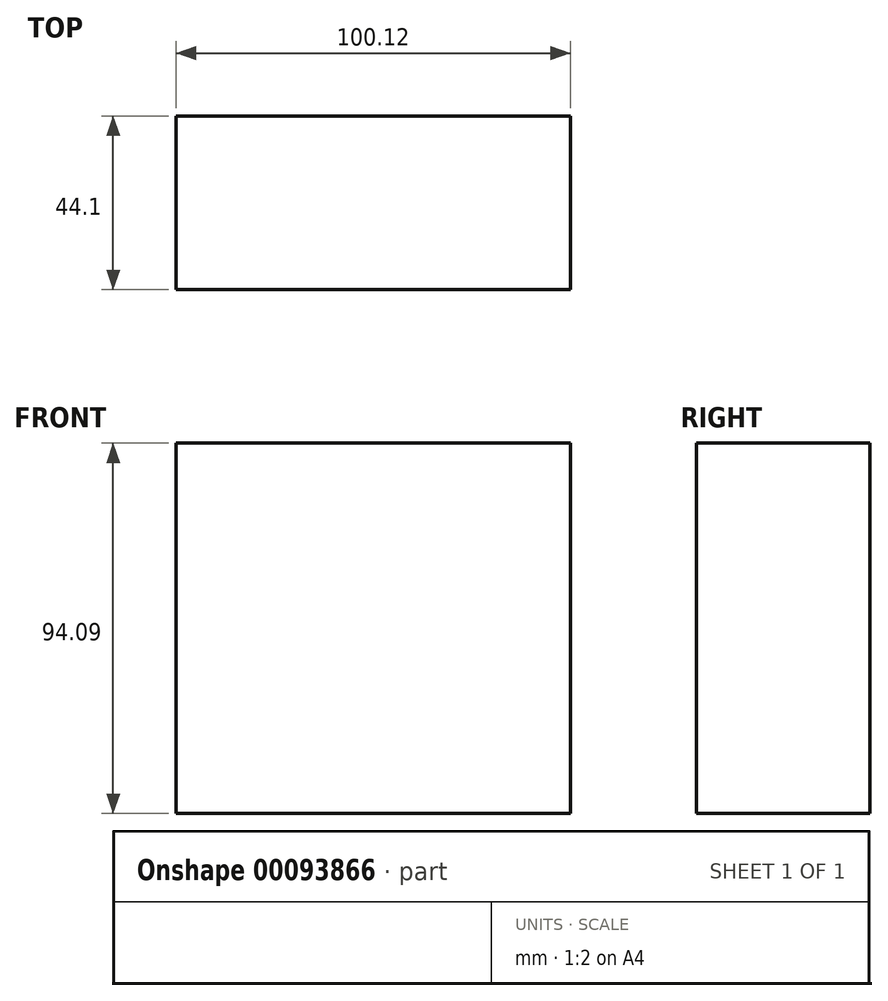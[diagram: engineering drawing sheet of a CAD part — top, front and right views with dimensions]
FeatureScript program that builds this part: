
annotation { "Feature Type Name" : "Feature", "Feature Type Description" : "" }
export const myFeature = defineFeature(function(context is Context, id is Id, definition is map)
    precondition{}
    {
        {
            var Q0;
            Q0=qCreatedBy(makeId("Top.planeOp"),FACE);
            var sketch = newSketch(context, id + "F0", { "sketchPlane" : qUnion([Q0])});
            skLineSegment(sketch, "E0.bottom", {"start": v(-26.52, 23.99) * mm, "end": v(73.6, 23.99) * mm});
            skLineSegment(sketch, "E0.top", {"start": v(-26.52, -20.11) * mm, "end": v(73.6, -20.11) * mm});
            skLineSegment(sketch, "E0.left", {"start": v(-26.52, 23.99) * mm, "end": v(-26.52, -20.11) * mm});
            skLineSegment(sketch, "E0.right", {"start": v(73.6, 23.99) * mm, "end": v(73.6, -20.11) * mm});
            skSolve(sketch);
        }
        {
            var Q0;
            Q0=makeQuery(id+"F0.imprint","IMPRINT",FACE,{"disambiguationData":[TD([[makeQuery(id+"F0.imprint","IMPRINT",EDGE,{"derivedFrom":sQuery(id+"F0.wireOp",EDGE,"E0.bottom")}),-1.0]])]});
            extrude(context, id + "F1", {"entities" : qUnion([Q0]), "depth" : 94.1 * mm});
        }
    });
